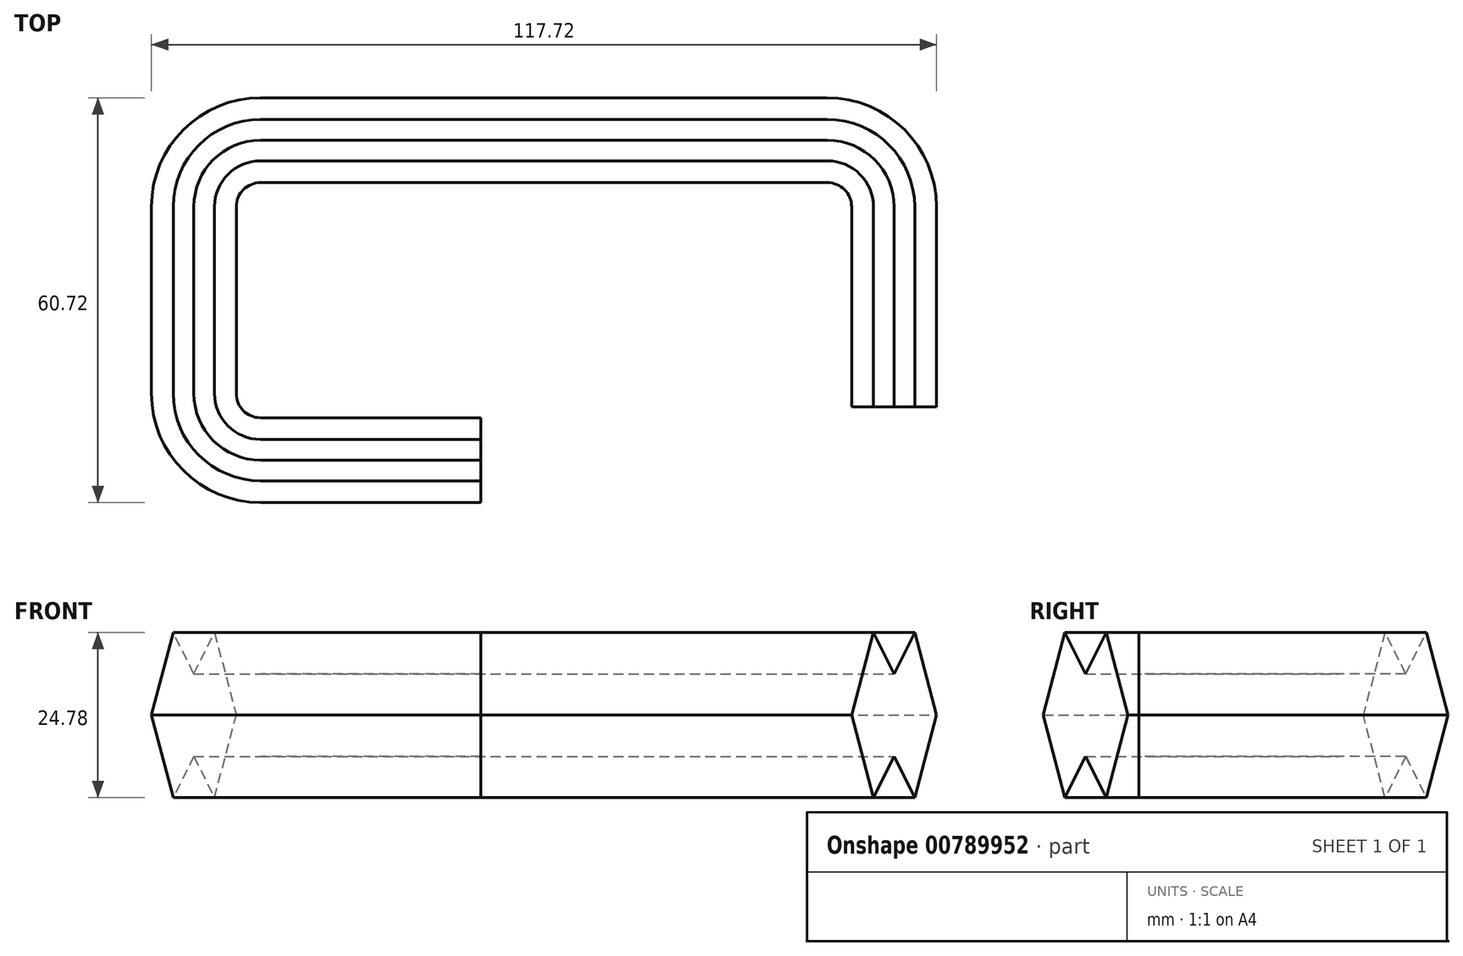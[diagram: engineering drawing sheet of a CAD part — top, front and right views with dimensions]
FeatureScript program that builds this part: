
annotation { "Feature Type Name" : "Feature", "Feature Type Description" : "" }
export const myFeature = defineFeature(function(context is Context, id is Id, definition is map)
    precondition{}
    {
        {
            var Q0;
            Q0=qCreatedBy(makeId("Right.planeOp"),FACE);
            var sketch = newSketch(context, id + "F0", { "sketchPlane" : qUnion([Q0])});
            skLineSegment(sketch, "E0", {"start": v(-3.1, 12.4) * mm, "end": v(-6.36, 0) * mm});
            skLineSegment(sketch, "E1", {"start": v(0, 6.2) * mm, "end": v(-3.1, 12.4) * mm});
            skPoint(sketch, "E1.startSnap0", {"position": v(-4.73, 6.2) * mm});
            skPoint(sketch, "E2.MirrorP", {"position": v(-4.73, -6.2) * mm});
            skLineSegment(sketch, "E3.MirrorCS", {"start": v(0, -6.2) * mm, "end": v(-3.1, -12.4) * mm});
            skLineSegment(sketch, "E4.MirrorCS", {"start": v(-3.1, -12.4) * mm, "end": v(-6.36, 0) * mm});
            skLineSegment(sketch, "E5.MirrorCS", {"start": v(0, 6.2) * mm, "end": v(3.1, 12.4) * mm});
            skLineSegment(sketch, "E6.MirrorCS", {"start": v(3.1, 12.4) * mm, "end": v(6.36, 0) * mm});
            skLineSegment(sketch, "E7.MirrorCS", {"start": v(3.1, -12.4) * mm, "end": v(6.36, 0) * mm});
            skLineSegment(sketch, "E8.MirrorCS", {"start": v(0, -6.2) * mm, "end": v(3.1, -12.4) * mm});
            skSolve(sketch);
        }
        {
            var Q0;
            Q0=qCreatedBy(makeId("Top.planeOp"),FACE);
            var sketch = newSketch(context, id + "F1", { "sketchPlane" : qUnion([Q0])});
            skLineSegment(sketch, "E9", {"start": v(0, 0) * mm, "end": v(-33.02, 0) * mm});
            skLineSegment(sketch, "E10", {"start": v(-43.02, 10) * mm, "end": v(-43.02, 38) * mm});
            skLineSegment(sketch, "E11", {"start": v(-33.02, 48) * mm, "end": v(51.98, 48) * mm});
            skLineSegment(sketch, "E12", {"start": v(61.98, 38) * mm, "end": v(61.98, 8) * mm});
            skPoint(sketch, "E13.visualSharp", {"position": v(-43.02, 0) * mm});
            skArc(sketch, "E13.filletArc", {"start": v(-43.02, 10) * mm, "mid": v(-40.1, 2.93) * mm, "end": v(-33.02, 0) * mm});
            skPoint(sketch, "E14.visualSharp", {"position": v(-43.02, 48) * mm});
            skArc(sketch, "E14.filletArc", {"start": v(-33.02, 48) * mm, "mid": v(-40.1, 45.07) * mm, "end": v(-43.02, 38) * mm});
            skPoint(sketch, "E15.visualSharp", {"position": v(61.98, 48) * mm});
            skArc(sketch, "E15.filletArc", {"start": v(61.98, 38) * mm, "mid": v(59.05, 45.07) * mm, "end": v(51.98, 48) * mm});
            skSolve(sketch);
        }
        {
            var Q0;
            Q0 = qSketchRegion(id + "F0", true);
            var Q1;
            Q1=sQuery(id+"F1.wireOp",EDGE,"E9");
            var Q2;
            Q2=sQuery(id+"F1.wireOp",EDGE,"E13.filletArc");
            var Q3;
            Q3=sQuery(id+"F1.wireOp",EDGE,"E10");
            var Q4;
            Q4=sQuery(id+"F1.wireOp",EDGE,"E14.filletArc");
            var Q5;
            Q5=sQuery(id+"F1.wireOp",EDGE,"E11");
            var Q6;
            Q6=sQuery(id+"F1.wireOp",EDGE,"E15.filletArc");
            var Q7;
            Q7=sQuery(id+"F1.wireOp",EDGE,"E12");
            sweep(context, id + "F2", {"profiles" : qUnion([Q0]), "path" : qUnion([Q1, Q2, Q3, Q4, Q5, Q6, Q7])});
        }
    });
